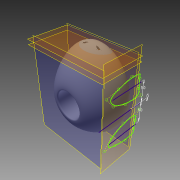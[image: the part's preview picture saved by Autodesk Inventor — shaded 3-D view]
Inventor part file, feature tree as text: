
AUTODESK INVENTOR PART (.ipt)
format: ipt  version: 2014 (Build 180170000, 170)  size: 1,119,744 bytes
history: native  units: mm
features: sketch x18, extrude x12, other x9, projected_geometry x5, fillet x3, mirror x3, loft x2, shell x2, chamfer x2
ambient origin geometry x8: Origin, YZ Plane, XZ Plane, XY Plane, X Axis, Y Axis, Z Axis, Center Point
bodies: Body1 (feature_tree)
feature tree (56):
  other  "body.ipt"
  other  "作業平面1"
  sketch  "スケッチ3"
  other  "作業平面4"
  sketch  "スケッチ6"
  loft  "ロフト2"
  extrude  "押し出し2"  [1 undecoded]
  fillet  "フィレット1"  Radius=65.0mm
  fillet  "フィレット2"  Radius=7.0mm
  fillet  "フィレット3"  Radius=80.388mm
  shell  "シェル2"  Thickness=6.6mm
  extrude  "押し出し3"  Depth=98.0mm
  extrude  "押し出し4"  Depth=5.0mm
  other  "作業平面5"
  extrude  "押し出し5"  Depth=10.0mm
  mirror  "ミラー1"
  loft  "ロフト3"
  shell  "シェル3"  Thickness=40.0mm
  other  "作業平面6"
  sketch  "スケッチ17"
  extrude  "押し出し10"  Depth=3.0mm
  extrude  "押し出し11"  Depth=3.0mm
  extrude  "押し出し12"  Depth=3.0mm
  chamfer  "面取り1"  Distance=1.8mm
  extrude  "押し出し13"  Depth=93.939mm
  mirror  "ミラー4"
  extrude  "押し出し14"  Depth=3.4mm
  other  "作業平面10"
  extrude  "押し出し15"  TaperAngle=0.0deg  [1 undecoded]
  mirror  "ミラー5"
  extrude  "押し出し16"  Depth=79.8mm
  extrude  "押し出し17"  TaperAngle=0.0deg  [1 undecoded]
  chamfer  "面取り2"  Distance=3.4mm
  other  "ソリッド1::body.ipt"
  other  "TaggingFeature1"
  sketch  "スケッチ8"
  sketch  "スケッチ10"
  sketch  "スケッチ11"
  projected_geometry  "投影ループ2"
  projected_geometry  "投影ループ3"
  sketch  "スケッチ12"
  sketch  "スケッチ14"
  sketch  "スケッチ15"
  sketch  "スケッチ16"
  sketch  "スケッチ22"
  sketch  "スケッチ23"
  projected_geometry  "投影ループ7"
  sketch  "スケッチ25"
  projected_geometry  "投影ループ8"
  sketch  "スケッチ26"
  sketch  "スケッチ27"
  sketch  "スケッチ30"
  sketch  "スケッチ31"
  sketch  "スケッチ32"
  projected_geometry  "投影ループ9"
  other  "ソリッド1"
note: 3 required parameter values undecoded (feature->parameter linkage not recoverable at this tier; creation-order binding heuristic only, values carry confidence <= 0.55)
